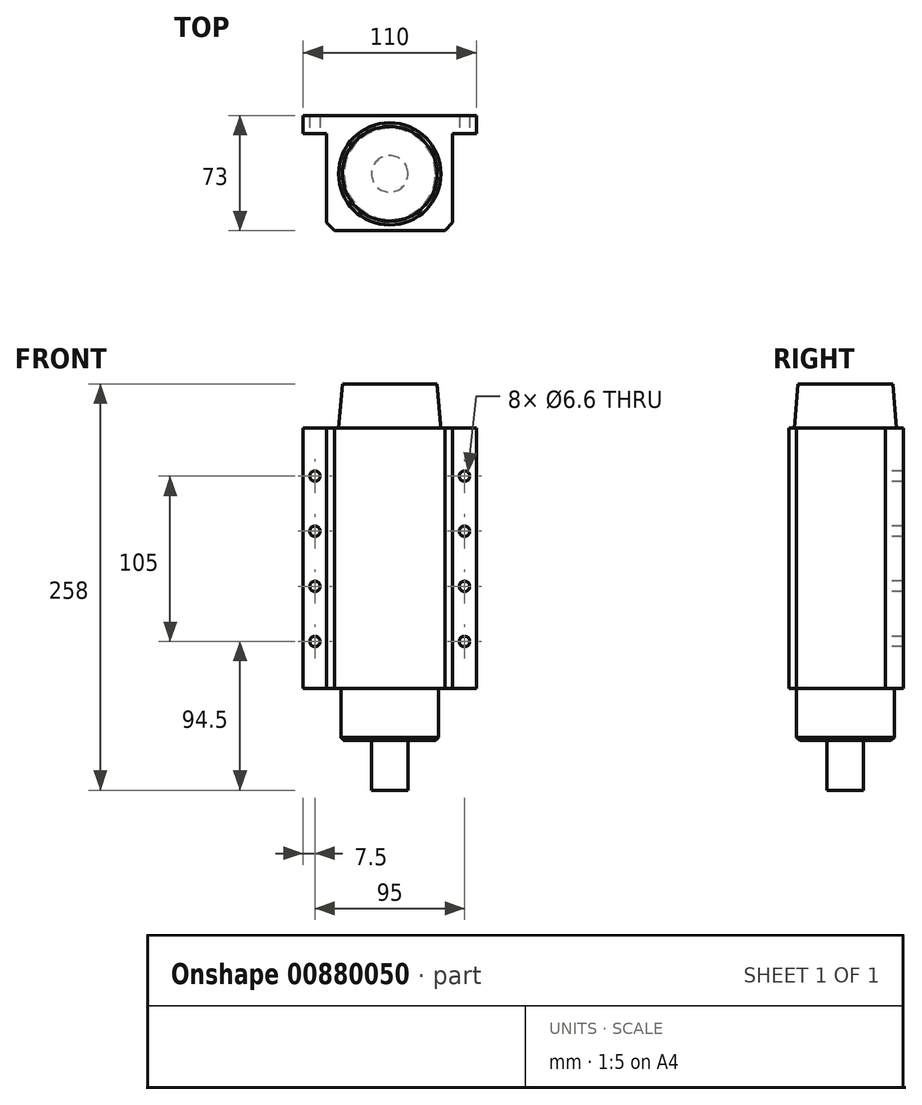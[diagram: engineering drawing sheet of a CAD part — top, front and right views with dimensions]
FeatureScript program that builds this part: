
annotation { "Feature Type Name" : "Feature", "Feature Type Description" : "" }
export const myFeature = defineFeature(function(context is Context, id is Id, definition is map)
    precondition{}
    {
        {
            var Q0;
            Q0=qCreatedBy(makeId("Top.planeOp"),FACE);
            var sketch = newSketch(context, id + "F0", { "sketchPlane" : qUnion([Q0])});
            skLineSegment(sketch, "E0", {"start": v(-55, 37) * mm, "end": v(0, 37) * mm});
            skLineSegment(sketch, "E1", {"start": v(0, -36) * mm, "end": v(-40, -36) * mm});
            skLineSegment(sketch, "E2", {"start": v(-40, -36) * mm, "end": v(-40, 25.5) * mm});
            skLineSegment(sketch, "E3", {"start": v(-40, 25.5) * mm, "end": v(-55, 25.5) * mm});
            skLineSegment(sketch, "E4", {"start": v(-55, 25.5) * mm, "end": v(-55, 37) * mm});
            skLineSegment(sketch, "E5", {"start": v(0, 47.06) * mm, "end": v(0, -52.64) * mm, "construction": true});
            skLineSegment(sketch, "E6.MirrorCS", {"start": v(0, -36) * mm, "end": v(40, -36) * mm});
            skLineSegment(sketch, "E7.MirrorCS", {"start": v(40, -36) * mm, "end": v(40, 25.5) * mm});
            skLineSegment(sketch, "E8.MirrorCS", {"start": v(40, 25.5) * mm, "end": v(55, 25.5) * mm});
            skLineSegment(sketch, "E9.MirrorCS", {"start": v(55, 25.5) * mm, "end": v(55, 37) * mm});
            skLineSegment(sketch, "E10.MirrorCS", {"start": v(55, 37) * mm, "end": v(0, 37) * mm});
            skSolve(sketch);
        }
        {
            var Q0;
            Q0=makeQuery(id+"F0.imprint","IMPRINT",FACE,{"disambiguationData":[TD([[makeQuery(id+"F0.imprint","IMPRINT",EDGE,{"derivedFrom":sQuery(id+"F0.wireOp",EDGE,"E0")}),-1.0]])]});
            extrude(context, id + "F1", {"entities" : qUnion([Q0]), "endBound" : BoundingType.SYMMETRIC, "depth" : 165.5 * mm, "offsetDistance" : 25 * mm});
        }
        {
            var Q0;
            Q0=makeQuery(id+"F1.opExtrude","SWEPT_EDGE",EDGE,{"disambiguationData":[OSD([sQuery(id+"F0.wireOp",EDGE,"E6.MirrorCS"),sQuery(id+"F0.wireOp",EDGE,"E7.MirrorCS")])]});
            var Q1;
            Q1=makeQuery(id+"F1.opExtrude","SWEPT_EDGE",EDGE,{"disambiguationData":[OSD([sQuery(id+"F0.wireOp",EDGE,"E1"),sQuery(id+"F0.wireOp",EDGE,"E2")])]});
            chamfer(context, id + "F2", {"entities" : qUnion([Q0, Q1]), "width" : 5 * mm, "tangentPropagation" : true});
        }
        {
            var Q0;
            Q0=makeQuery(id+"F1.opExtrude","CAP_FACE",FACE,{"disambiguationData":[OSD([sQuery(id+"F0.wireOp",EDGE,"E0"),sQuery(id+"F0.wireOp",EDGE,"E1"),sQuery(id+"F0.wireOp",EDGE,"E2"),sQuery(id+"F0.wireOp",EDGE,"E3"),sQuery(id+"F0.wireOp",EDGE,"E4"),sQuery(id+"F0.wireOp",EDGE,"E6.MirrorCS"),sQuery(id+"F0.wireOp",EDGE,"E7.MirrorCS"),sQuery(id+"F0.wireOp",EDGE,"E8.MirrorCS"),sQuery(id+"F0.wireOp",EDGE,"E9.MirrorCS"),sQuery(id+"F0.wireOp",EDGE,"E10.MirrorCS")])],"isStart":true});
            var sketch = newSketch(context, id + "F3", { "sketchPlane" : qUnion([Q0])});
            skCircle(sketch, "E11", {"center": v(0, 0) * mm, "radius": 31 * mm});
            skSolve(sketch);
        }
        {
            var Q0;
            Q0=makeQuery(id+"F3.imprint","IMPRINT",FACE,{"disambiguationData":[TD([[makeQuery(id+"F3.imprint","IMPRINT",EDGE,{"derivedFrom":sQuery(id+"F3.wireOp",EDGE,"E11")}),1.0]])]});
            extrude(context, id + "F4", {"entities" : qUnion([Q0]), "operationType" : NewBodyOperationType.ADD, "depth" : 33 * mm, "offsetDistance" : 25 * mm});
        }
        {
            var Q0;
            Q0=makeQuery(id+"F4.opExtrude","CAP_EDGE",EDGE,{"disambiguationData":[OSD([sQuery(id+"F3.wireOp",EDGE,"E11")])],"isStart":false});
            chamfer(context, id + "F5", {"entities" : qUnion([Q0]), "width" : 2 * mm, "tangentPropagation" : true});
        }
        {
            var Q0;
            Q0=makeQuery(id+"F4.opExtrude","CAP_FACE",FACE,{"disambiguationData":[OSD([sQuery(id+"F3.wireOp",EDGE,"E11")])],"isStart":false});
            var sketch = newSketch(context, id + "F6", { "sketchPlane" : qUnion([Q0])});
            skCircle(sketch, "E12", {"center": v(0, 0) * mm, "radius": 11.6 * mm});
            skSolve(sketch);
        }
        {
            var Q0;
            Q0=makeQuery(id+"F6.imprint","IMPRINT",FACE,{"disambiguationData":[TD([[makeQuery(id+"F6.imprint","IMPRINT",EDGE,{"derivedFrom":sQuery(id+"F6.wireOp",EDGE,"E12")}),1.0]])]});
            extrude(context, id + "F7", {"entities" : qUnion([Q0]), "operationType" : NewBodyOperationType.ADD, "depth" : 31.5 * mm, "offsetDistance" : 25 * mm});
        }
        {
            var Q0;
            Q0=makeQuery(id+"F1.opExtrude","CAP_FACE",FACE,{"disambiguationData":[OSD([sQuery(id+"F0.wireOp",EDGE,"E0"),sQuery(id+"F0.wireOp",EDGE,"E1"),sQuery(id+"F0.wireOp",EDGE,"E2"),sQuery(id+"F0.wireOp",EDGE,"E3"),sQuery(id+"F0.wireOp",EDGE,"E4"),sQuery(id+"F0.wireOp",EDGE,"E6.MirrorCS"),sQuery(id+"F0.wireOp",EDGE,"E7.MirrorCS"),sQuery(id+"F0.wireOp",EDGE,"E8.MirrorCS"),sQuery(id+"F0.wireOp",EDGE,"E9.MirrorCS"),sQuery(id+"F0.wireOp",EDGE,"E10.MirrorCS")])],"isStart":false});
            var sketch = newSketch(context, id + "F8", { "sketchPlane" : qUnion([Q0])});
            skCircle(sketch, "E13", {"center": v(0, 0) * mm, "radius": 32.5 * mm});
            skSolve(sketch);
        }
        {
            var Q0;
            Q0=makeQuery(id+"F8.imprint","IMPRINT",FACE,{"disambiguationData":[TD([[makeQuery(id+"F8.imprint","IMPRINT",EDGE,{"derivedFrom":sQuery(id+"F8.wireOp",EDGE,"E13")}),1.0]])]});
            extrude(context, id + "F9", {"entities" : qUnion([Q0]), "operationType" : NewBodyOperationType.ADD, "depth" : 28 * mm, "offsetDistance" : 25 * mm, "hasDraft" : true, "draftAngle" : 5 * degree, "draftPullDirection" : true});
        }
        {
            var Q0;
            Q0=makeQuery(id+"F1.opExtrude","SWEPT_FACE",FACE,{"disambiguationData":[OSD([sQuery(id+"F0.wireOp",EDGE,"E3")])]});
            var sketch = newSketch(context, id + "F10", { "sketchPlane" : qUnion([Q0])});
            skPoint(sketch, "E14", {"position": v(-47.5, 52.25) * mm});
            skPoint(sketch, "E15", {"position": v(-47.5, 17.25) * mm});
            skPoint(sketch, "E16", {"position": v(-47.5, -17.75) * mm});
            skPoint(sketch, "E17", {"position": v(-47.5, -52.75) * mm});
            skPoint(sketch, "E18", {"position": v(47.5, -52.75) * mm});
            skPoint(sketch, "E19", {"position": v(47.5, -17.75) * mm});
            skPoint(sketch, "E20", {"position": v(47.5, 17.25) * mm});
            skPoint(sketch, "E21", {"position": v(47.5, 52.25) * mm});
            skSolve(sketch);
        }
        {
            var Q0;
            Q0=sQuery(id+"F10.wireOp",VERTEX,"E14");
            var Q1;
            Q1=sQuery(id+"F10.wireOp",VERTEX,"E15");
            var Q2;
            Q2=sQuery(id+"F10.wireOp",VERTEX,"E16");
            var Q3;
            Q3=sQuery(id+"F10.wireOp",VERTEX,"E17");
            var Q4;
            Q4=sQuery(id+"F10.wireOp",VERTEX,"E21");
            var Q5;
            Q5=sQuery(id+"F10.wireOp",VERTEX,"E20");
            var Q6;
            Q6=sQuery(id+"F10.wireOp",VERTEX,"E19");
            var Q7;
            Q7=sQuery(id+"F10.wireOp",VERTEX,"E18");
            var Q8;
            Q8=makeQuery(id+"F1.opExtrude","SWEPT_BODY",BODY,{"disambiguationData":[OSD([sQuery(id+"F0.wireOp",EDGE,"E0"),sQuery(id+"F0.wireOp",EDGE,"E1"),sQuery(id+"F0.wireOp",EDGE,"E2"),sQuery(id+"F0.wireOp",EDGE,"E3"),sQuery(id+"F0.wireOp",EDGE,"E4"),sQuery(id+"F0.wireOp",EDGE,"E6.MirrorCS"),sQuery(id+"F0.wireOp",EDGE,"E7.MirrorCS"),sQuery(id+"F0.wireOp",EDGE,"E8.MirrorCS"),sQuery(id+"F0.wireOp",EDGE,"E9.MirrorCS"),sQuery(id+"F0.wireOp",EDGE,"E10.MirrorCS")])]});
            hole(context, id + "F11", {"style" : HoleStyle.SIMPLE, "endStyle" : HoleEndStyle.THROUGH, "standardTappedOrClearance" : lookupTablePath({ "standard" : "ISO", "fit" : "Normal", "size" : "M6", "type" : "Clearance" }), "standardBlindInLast" : lookupTablePath({ "fit" : "Standard", "standard" : "ISO", "size" : "M6", "type" : "Clearance" }), "holeDiameter" : 6.6 * mm, "majorDiameter" : 5 * mm, "isTappedThrough" : true, "tappedDepth" : 12 * mm, "tapClearance" : 3, "locations" : qUnion([Q0, Q1, Q2, Q3, Q4, Q5, Q6, Q7]), "scope" : qUnion([Q8])});
        }
    });
